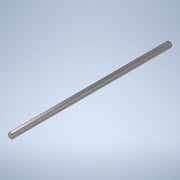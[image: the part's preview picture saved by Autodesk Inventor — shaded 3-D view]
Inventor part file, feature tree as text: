
AUTODESK INVENTOR PART (.ipt)
format: ipt  version: 2020 (Build 240168000, 168)  size: 103,936 bytes
history: native  units: in
note: dims shown in document units (in); Inventor stores cm internally (conversion verified against a paired STEP export)
features: extrude x1, sketch x1
ambient origin geometry x8: Origin, YZ Plane, XZ Plane, XY Plane, X Axis, Y Axis, Z Axis, Center Point
bodies: Solid1 (feature_tree)
feature tree (2):
  extrude  "Extrusion1"  Depth=17.0in TaperAngle=0.0deg
  sketch  "Sketch1"  dims[d0=0.5in d1=17.0in d2=0.0in]
